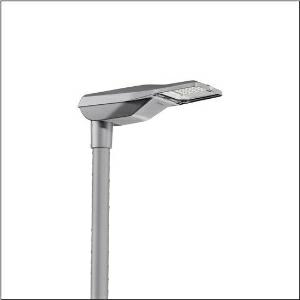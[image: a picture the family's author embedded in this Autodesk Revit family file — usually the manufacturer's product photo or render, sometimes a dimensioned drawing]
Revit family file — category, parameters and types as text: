
# Revit family: streetlight_sl_21_iq_micro___p0_8ab_5xe1r31g08cb_4e53
name_source: partatom
category: Lighting Fixtures
units: mm (PartAtom-declared; Revit-internal decimal feet)

## family parameters
Cut with Voids When Loaded = No
Host = Face
Light Source = No
Part Type = Normal
Room Calculation Point = No
Round Connector Dimension = Use Diameter
Shared = No

## types (1)
- --- (1 x LED, 2510 lm, 19.4 W, 3000K)
    Apparent Load = 19 VA
    CIE Flux Codes = 36 71 98 100 100
    Color Rendering = 70
    Color Temperature = 3000K
    Default Elevation = 1800 mm
    Description = Streetlight SL 21 iQ micro, mast luminaire, primary light control with lens, of PMMA, primary optical cover: cover, of toughened safety glass, transparent, light distribution: P0.8aB, light emission: direct distribution, primary light characteristic: asymmetric, installation type: post-top, side-entry, LED, High Power LED, rated luminous flux: 2.510lm, luminous efficacy: 129lm/W, light colour: 730, colour temperature: 3000K, control gear: iQ Street-Remote, control: pre-setting: linear dimming characteristic, Street-Remote, Auto-Match, Temp-Guard, Lumen-Switch, Night-Set, Smart-Wire, Light-Fading, Desk-Remote (wireless, voltage-free reading and setting of iQ features in the workshop via application-optimized NFC function/RFID function), optimised constant luminous flux control (CLO 2.0), mains connection: 220..240V, AC, 50/60Hz, start of lifetime: 19W, end of service life: 20W, reduction: 10W, luminaire housing, of diecast aluminium, powder-coated, SITECO metallic grey (DB 702S), corrosivity category C5 high according to DIN EN ISO 12944, please order mast flange separately, inclination adjustable: 0°, 5°, 10°, 15°, sealing non-destructively replaceable, multi-level sealing system, length: 528mm, width: 235mm, height: 110mm, mast flange for spigot size: 42mm (side-entry): 5XC10008XM4, 60/48mm (side-entry/post-top): 5XC10108XM2, 76/60mm (side-entry/post-top): 5XC10108XM1, protection rating (complete): IP66, insulation class (complete): insulation class II (safety insulation), certification: CE, ENEC, ENEC+, VDE, impact resistance: IK10, permissible operating ambient temperature for outdoor applications: -40..+50°C, standard-compliant lighting for roads and squares, packaging unit: 1 piece

Light Distribution: P0.8aB
    Height = 110 mm
    Lamp = 1 x LED
    Lamp Light Flux = 2510 lm
    Lamp Power = 19.4 W
    Lamp count = 1
    Length = 528 mm
    Luminous efficacy = 129 lm/W
    Manufacturer = Siteco
    ModVariant = No
    Model = 5XE1R31G08CB
    Number of Poles = 1
    OnlyDefault = Yes
    Power Factor = 1
    Product Name = Streetlight SL 21 iQ micro | P0.8aB
    Product group = mast luminaire | pylon top
    ProductGroupID = 6100
    Protection Class = Protection class II
    Protection Degree = IP 66
    RLX_Detail_Level = 1
    RLX_Emergency_Light_Flux = 0 lm
    RLX_Emergency_Type = 0
    RLX_Emergency_Type_DB = No
    RlxData = <blob elided: 98977 chars, md5=b7304ca6>
    Socket = socket
    Standby Power = 0 W
    System Light Flux = 2510 lm
    System Power = 19 W
    Type Comments = factory setting: luminous flux: 100 % | dim-lin: 254 | 387 mA
    Type Image = l_1006881.jpg
    URL = http://relux.com
    VarID = @adj_082453
    Voltage = 0 V
    Weight = 0.00 kg
    Width = 235 mm

## geometry (parser evidence)
native form markers: Blend x4, Sweep x9
no freeform markers — native parametric forms only
